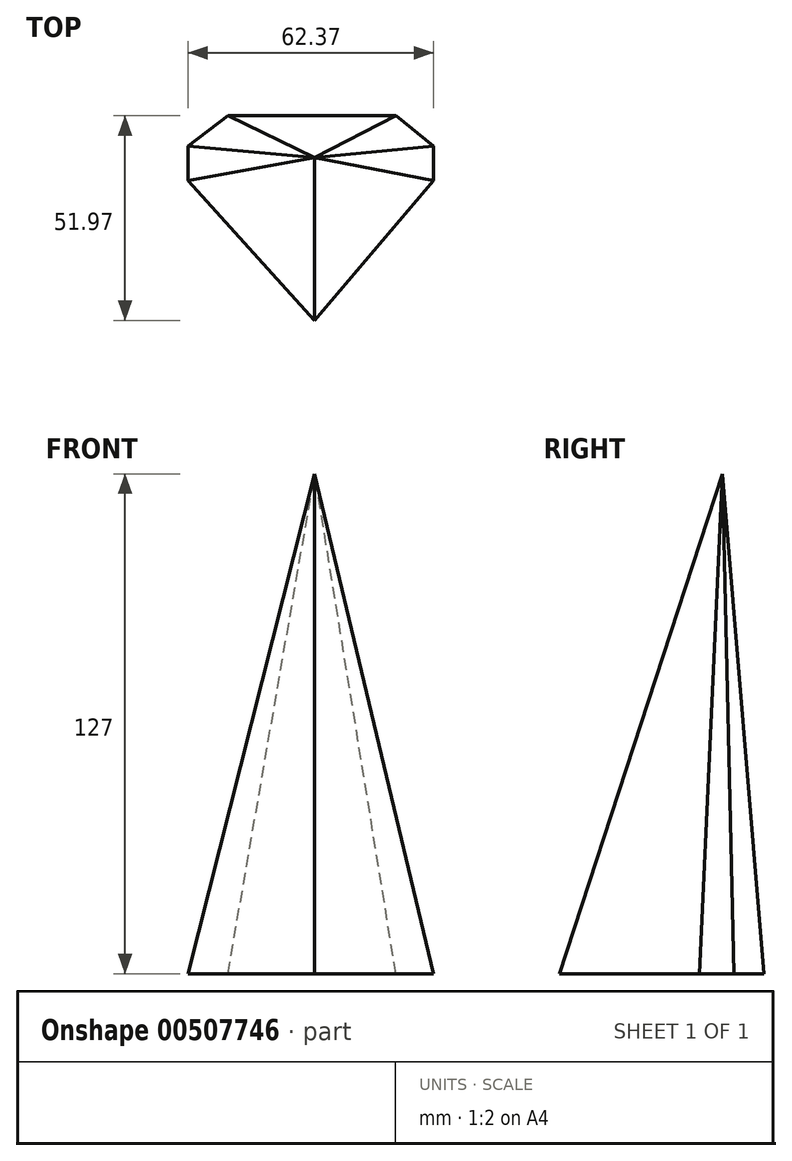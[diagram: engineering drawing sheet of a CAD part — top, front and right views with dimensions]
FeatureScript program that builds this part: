
annotation { "Feature Type Name" : "Feature", "Feature Type Description" : "" }
export const myFeature = defineFeature(function(context is Context, id is Id, definition is map)
    precondition{}
    {
        {
            var Q0;
            Q0=qCreatedBy(makeId("Top.planeOp"),FACE);
            var sketch = newSketch(context, id + "F0", { "sketchPlane" : qUnion([Q0])});
            skLineSegment(sketch, "E0", {"start": v(-32.18, 0) * mm, "end": v(-32.18, 8.74) * mm});
            skLineSegment(sketch, "E1", {"start": v(-32.18, 8.74) * mm, "end": v(-22.06, 16.4) * mm});
            skLineSegment(sketch, "E2", {"start": v(-22.06, 16.4) * mm, "end": v(20.61, 16.4) * mm});
            skLineSegment(sketch, "E3", {"start": v(20.61, 16.4) * mm, "end": v(30.19, 8.74) * mm});
            skLineSegment(sketch, "E4", {"start": v(30.19, 8.74) * mm, "end": v(30.19, 0) * mm});
            skLineSegment(sketch, "E5", {"start": v(-32.18, 0) * mm, "end": v(0, -35.57) * mm});
            skLineSegment(sketch, "E6", {"start": v(30.19, 0) * mm, "end": v(0, -35.57) * mm});
            skSolve(sketch);
        }
        {
            var Q0;
            Q0=qCreatedBy(makeId("Top.planeOp"),FACE);
            cPlane(context, id + "F1", {"entities" : qUnion([Q0]), "cplaneType" : CPlaneType.OFFSET, "offset" : 127 * mm, "width" : 152.4 * mm, "height" : 152.4 * mm});
        }
        {
            var Q0;
            Q0=qCreatedBy(id+"F1.planeOp",FACE);
            var sketch = newSketch(context, id + "F2", { "sketchPlane" : qUnion([Q0])});
            skPoint(sketch, "E7", {"position": v(0, 5.78) * mm});
            skSolve(sketch);
        }
        {
            var Q0;
            Q0=makeQuery(id+"F0.imprint","IMPRINT",FACE,{"disambiguationData":[TD([[makeQuery(id+"F0.imprint","IMPRINT",EDGE,{"derivedFrom":sQuery(id+"F0.wireOp",EDGE,"E0")}),-1.0]])]});
            var Q1;
            Q1=sQuery(id+"F2.wireOp",VERTEX,"E7");
            loft(context, id + "F3", {"sheetProfilesArray" : [{ "sheetProfileEntities" : qUnion([Q0]) }, { "sheetProfileEntities" : qUnion([Q1]) }]});
        }
    });
